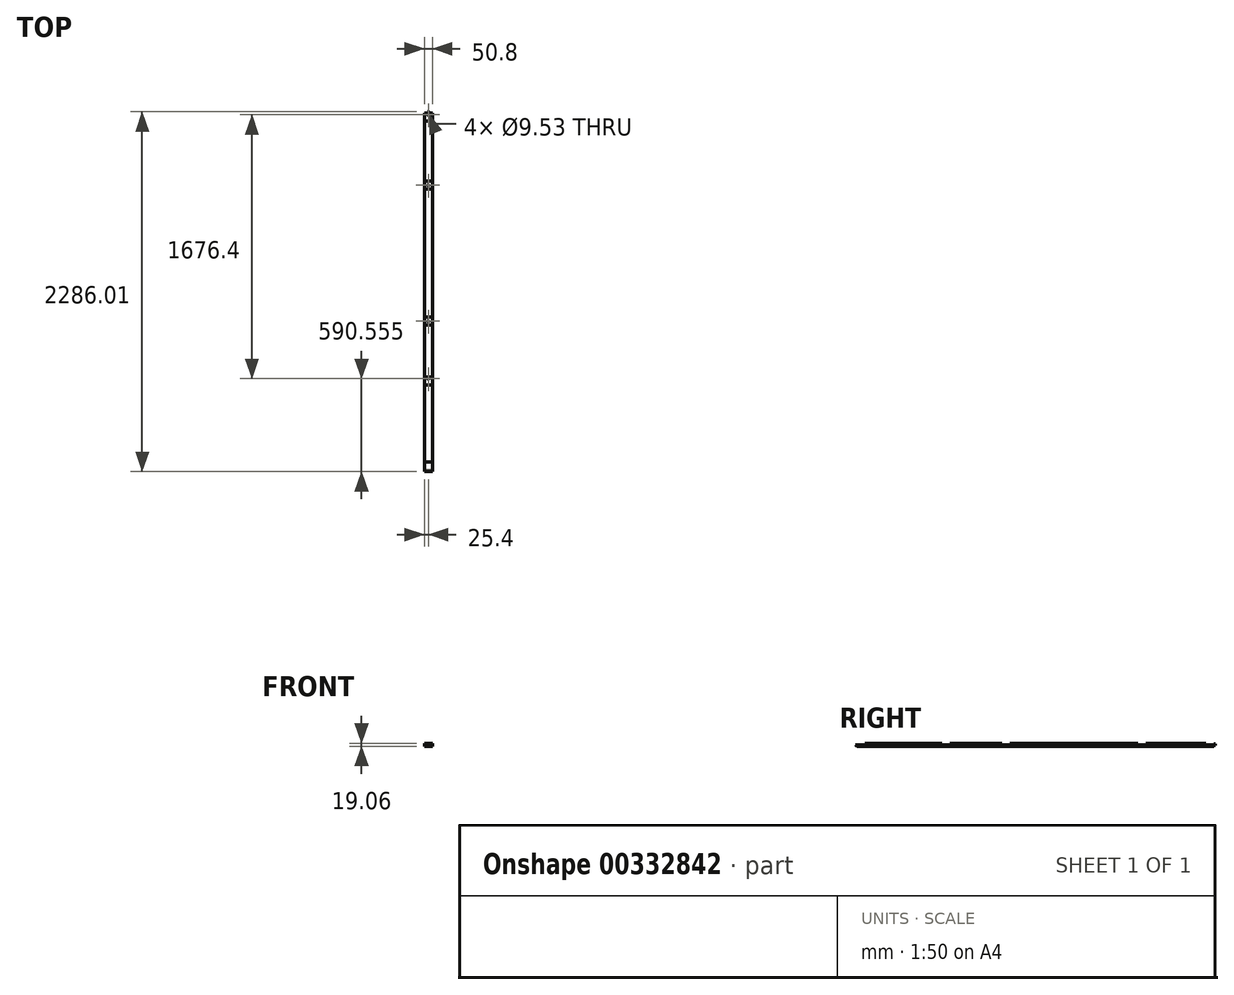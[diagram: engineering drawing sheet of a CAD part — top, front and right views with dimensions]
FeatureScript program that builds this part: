
annotation { "Feature Type Name" : "Feature", "Feature Type Description" : "" }
export const myFeature = defineFeature(function(context is Context, id is Id, definition is map)
    precondition{}
    {
        {
            var Q0;
            Q0=qCreatedBy(makeId("Right.planeOp"),FACE);
            var sketch = newSketch(context, id + "F0", { "sketchPlane" : qUnion([Q0])});
            skLineSegment(sketch, "E0.top", {"start": v(2133.6, -9.52) * mm, "end": v(2133.6, 0) * mm});
            skLineSegment(sketch, "E0.right", {"start": v(0, 9.52) * mm, "end": v(406.4, 9.53) * mm});
            skLineSegment(sketch, "E1.top", {"start": v(2082.8, 9.53) * mm, "end": v(2082.8, 0) * mm});
            skLineSegment(sketch, "E1.right", {"start": v(2133.6, 0) * mm, "end": v(2082.8, 0) * mm});
            skLineSegment(sketch, "E2", {"start": v(2133.6, -9.52) * mm, "end": v(-33.3, -9.53) * mm});
            skLineSegment(sketch, "E3.right", {"start": v(2082.8, 0) * mm, "end": v(2082.8, 0) * mm});
            skLineSegment(sketch, "E4.trimOffspring", {"start": v(2082.8, 9.53) * mm, "end": v(2082.8, 9.53) * mm});
            skLineSegment(sketch, "E5.top", {"start": v(1651, 9.53) * mm, "end": v(1651, 0) * mm});
            skLineSegment(sketch, "E5.right", {"start": v(1701.8, 0) * mm, "end": v(1651, 0) * mm});
            skLineSegment(sketch, "E6.bottom", {"start": v(838.2, 9.53) * mm, "end": v(838.2, 0) * mm});
            skLineSegment(sketch, "E6.top", {"start": v(787.4, 9.53) * mm, "end": v(787.4, 0) * mm});
            skLineSegment(sketch, "E6.right", {"start": v(838.2, 0) * mm, "end": v(787.4, 0) * mm});
            skPoint(sketch, "E6.left.start.orphan", {"position": v(838.2, 48.5) * mm});
            skPoint(sketch, "E7.orphan", {"position": v(787.4, 48.5) * mm});
            skLineSegment(sketch, "E8.trimOffspring", {"start": v(838.2, 9.53) * mm, "end": v(1651, 9.53) * mm});
            skLineSegment(sketch, "E9", {"start": v(1701.8, 0) * mm, "end": v(1701.8, 9.53) * mm});
            skLineSegment(sketch, "E10.trimOffspring", {"start": v(1701.8, 9.53) * mm, "end": v(2082.8, 9.53) * mm});
            skLineSegment(sketch, "E11", {"start": v(0, 9.52) * mm, "end": v(-82.55, 9.52) * mm});
            skLineSegment(sketch, "E12", {"start": v(-142.88, 0) * mm, "end": v(-133.35, -9.53) * mm});
            skLineSegment(sketch, "E13", {"start": v(-33.3, -9.53) * mm, "end": v(-133.35, -9.53) * mm});
            skPoint(sketch, "E14.start.orphan", {"position": v(431.8, 9.53) * mm});
            skLineSegment(sketch, "E15.top", {"start": v(406.4, 0) * mm, "end": v(457.2, 0) * mm});
            skLineSegment(sketch, "E15.left", {"start": v(406.4, 9.53) * mm, "end": v(406.4, 0) * mm});
            skLineSegment(sketch, "E15.right", {"start": v(457.2, 9.53) * mm, "end": v(457.2, 0) * mm});
            skLineSegment(sketch, "E16.trimOffspring", {"start": v(457.2, 9.53) * mm, "end": v(787.4, 9.53) * mm});
            skLineSegment(sketch, "E17.top", {"start": v(-142.88, 0) * mm, "end": v(-82.55, 0) * mm});
            skLineSegment(sketch, "E17.right", {"start": v(-82.55, 9.52) * mm, "end": v(-82.55, 0) * mm});
            skPoint(sketch, "E18.orphan", {"position": v(-152.4, 9.52) * mm});
            skSolve(sketch);
        }
        {
            var Q0;
            Q0=qSketchRegion(id+"F0",true);
            extrude(context, id + "F1", {"entities" : qUnion([Q0]), "endBound" : BoundingType.SYMMETRIC, "depth" : 50.8 * mm});
        }
        {
            var Q0;
            Q0=qCreatedBy(makeId("Front.planeOp"),FACE);
            cPlane(context, id + "F2", {"entities" : qUnion([Q0]), "cplaneType" : CPlaneType.OFFSET, "offset" : 2133.6 * mm, "oppositeDirection" : true, "width" : 152.4 * mm, "height" : 152.4 * mm});
        }
        {
            var Q0;
            Q0=qCreatedBy(id+"F2.planeOp",FACE);
            var sketch = newSketch(context, id + "F3", { "sketchPlane" : qUnion([Q0])});
            skCircle(sketch, "E19", {"center": v(0, 0) * mm, "radius": 4.76 * mm});
            skSolve(sketch);
        }
        {
            var Q0;
            Q0=qSketchRegion(id+"F3",true);
            extrude(context, id + "F4", {"entities" : qUnion([Q0]), "operationType" : NewBodyOperationType.ADD, "oppositeDirection" : true, "depth" : 9.52 * mm});
        }
        {
            var Q0;
            Q0=qCreatedBy(makeId("Top.planeOp"),FACE);
            var sketch = newSketch(context, id + "F5", { "sketchPlane" : qUnion([Q0])});
            skCircle(sketch, "E20", {"center": v(0, 447.67) * mm, "radius": 4.76 * mm});
            skCircle(sketch, "E21", {"center": v(0, 812.8) * mm, "radius": 4.76 * mm});
            skCircle(sketch, "E22", {"center": v(0, 1676.4) * mm, "radius": 4.76 * mm});
            skCircle(sketch, "E23", {"center": v(0, 2124.07) * mm, "radius": 4.76 * mm});
            skSolve(sketch);
        }
        {
            var Q0;
            Q0=qSketchRegion(id+"F5",true);
            extrude(context, id + "F6", {"entities" : qUnion([Q0]), "operationType" : NewBodyOperationType.REMOVE, "oppositeDirection" : true, "depth" : 25.4 * mm});
        }
    });
